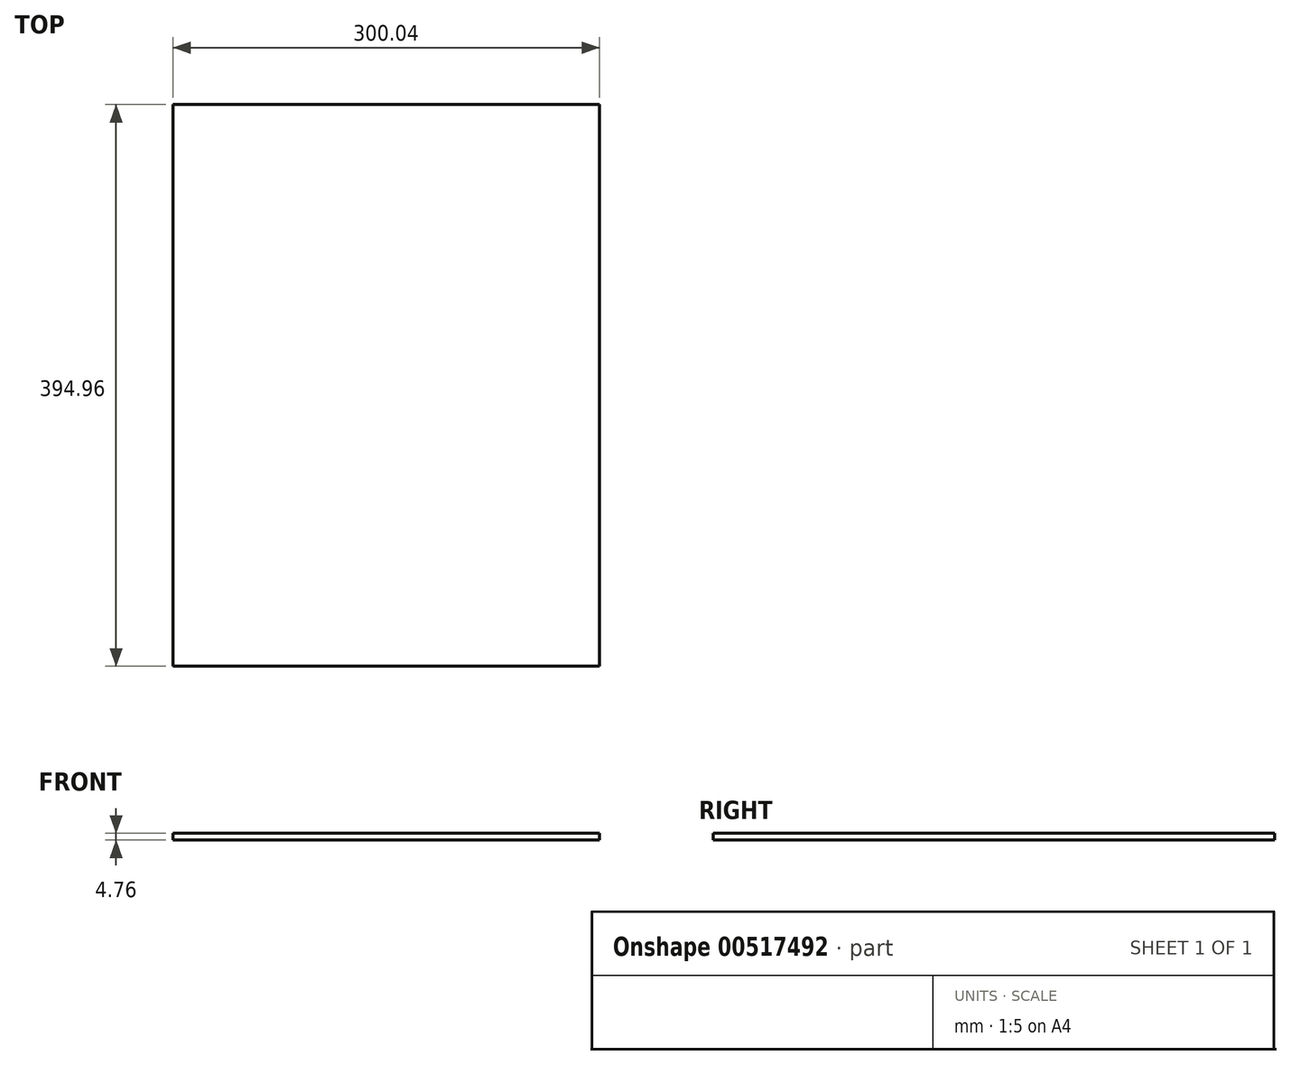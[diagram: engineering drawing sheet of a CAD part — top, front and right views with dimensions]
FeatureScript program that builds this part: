
annotation { "Feature Type Name" : "Feature", "Feature Type Description" : "" }
export const myFeature = defineFeature(function(context is Context, id is Id, definition is map)
    precondition{}
    {
        {
            var Q0;
            Q0=qCreatedBy(makeId("Top.planeOp"),FACE);
            var sketch = newSketch(context, id + "F0", { "sketchPlane" : qUnion([Q0])});
            skLineSegment(sketch, "E0.bottom", {"start": v(150.02, -197.48) * mm, "end": v(-150.02, -197.49) * mm});
            skLineSegment(sketch, "E0.top", {"start": v(150.02, 197.49) * mm, "end": v(-150.02, 197.48) * mm});
            skLineSegment(sketch, "E0.left", {"start": v(150.02, -197.48) * mm, "end": v(150.02, 197.49) * mm});
            skLineSegment(sketch, "E0.right", {"start": v(-150.02, -197.49) * mm, "end": v(-150.02, 197.49) * mm});
            skPoint(sketch, "E0.middle", {"position": v(0, 0) * mm});
            skSolve(sketch);
        }
        {
            var Q0;
            Q0=makeQuery(id+"F0.imprint","IMPRINT",FACE,{"disambiguationData":[TD([[makeQuery(id+"F0.imprint","IMPRINT",EDGE,{"derivedFrom":sQuery(id+"F0.wireOp",EDGE,"E0.bottom")}),-1.0]])]});
            extrude(context, id + "F1", {"entities" : qUnion([Q0]), "depth" : 4.76 * mm, "offsetDistance" : 25.4 * mm});
        }
    });
